# Revit family: 57-SUBCJ GF LVM MONOC KORAL MEDIA
name_source: partatom
category: Aparatos sanitarios
revit_build: Autodesk Revit 2018 (Build: 20170223_1515(x64)
units: mm (PartAtom-declared; Revit-internal decimal feet)

## family parameters
Anfitrión = Cara
Compartido = No
Corte con vacíos al cargar = No
Cota de conector redondo = Diámetro de uso
Número OmniClass = 23.45.55.17
Punto de cálculo de habitación = No
Tipo de pieza = Normal
Título OmniClass = Mixing Faucets

## types (1)
- 57-SUBCJ GF LVM MONOC KORAL MEDIA
    Acabado = Brillante
    Accionamiento = Manual
    Ahorro de Agua = Ahorro de agua (8,3l/min.) cumple con la norma NTC 1644
    Altura Nominal = 182.3
    Ancho Nominal = 44.8
    Características = Diseño exclusivo de formas limpias y estilizadas, tecnología Ecostream para ahorro de agua, chorro inclinado y espumoso, ideal para lavamanos de mesón integrado sobreponer o incriustar, manija que facilita la mexcla de agua fría y caliente
    Caudal = Promedio 4,8l/min. 60 psi
    Color = Cromo
    Consumo de agua = 8,3l/min.
    Cumplimiento de Norma = Ahorro de agua (8,3l/min.) cumple norma NTC 1644
    Código de montaje = D2010
    Descripción = Plumbing Fixtures
    Descripción IFC = Koral Lavamanos monocontrol medio
    Descripción de la garantía = Garantía de 30 años por defectos de fabricación, garantía de 5 años en acabados.
    Diámetro de conexión de entrada = 1/2 Pulg.
    Duración Garantía Partes = 30
    Duración Garantía Unidad = Años
    Duración Unidad = Años
    Elevación por defecto = 0 mm  [stored 0 ft]
    Fabricante = www.corona.com.co
    Forma = Cilíndrica
    Información del Producto = https://corona.co
    Logitud Nominal = 177.8
    Material Acabado = Cromo-Corona
    Material de Fabricación = Latón
    Nombre = Grifería Lavamanos Koral
    Nombre del Fabricante = Corona
    Número Modelo = KO1010001
    Presión Máxima = 125 psi
    Presión mínima = 20 psi
    Requerimientos Accesibilidad = Manual
    Responsable Garantías Partes = www.corona.com.co
    Tamaño = 177,8 x 44,8 x 182,3
    Tiempo Útil = 30
    Tipo de activo = Fijo
    Tráfico = Residencial
    Vida útil = Unidad de cierre 500000
    Vida útil unidad = Ciclos

note: [stored X ft] marks values corroborated as IEEE doubles in the binary element streams (Revit-internal decimal feet)

## geometry (parser evidence)
native form markers: Sweep x2
no freeform markers — native parametric forms only
